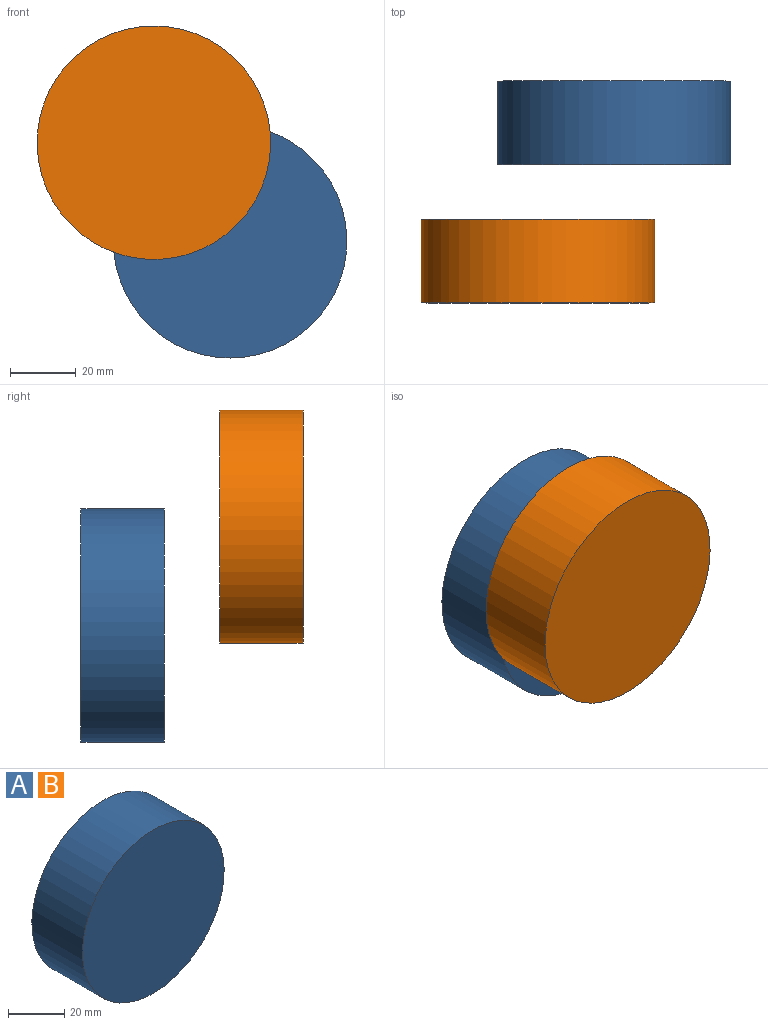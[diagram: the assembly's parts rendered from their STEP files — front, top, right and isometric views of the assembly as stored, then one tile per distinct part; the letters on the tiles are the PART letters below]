
ASSEMBLY  parts=2 mates=1
PART A: 3 faces, bbox 71.1x25.4x71.1 mm
  f0: cylinder r=35.54mm len=71.08mm, axis (0,1,0), area 5671.8mm2, adj f1,f2
  f1: plane 71.08x71.08mm, normal (0,-1,0), area 3968mm2, adj f0
  f2: plane 71.08x71.08mm, normal (0,1,0), area 3968mm2, adj f0
PART B: same geometry as A
PLACE A at identity
PLACE B rot(axis=(1,0,0),180deg) t=(-23.2,-42.2,30)mm
MATE parallel B.f0 <-> A.f0  axis (0,1,0) through (-23.2,-29.5,30)mm
